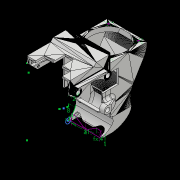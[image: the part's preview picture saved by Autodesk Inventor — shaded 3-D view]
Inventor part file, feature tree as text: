
AUTODESK INVENTOR PART (.ipt)
format: ipt  version: 2018.2 (Build 222227000, 227)  size: 11,716,096 bytes
history: native  units: mm
features: extrude x61, sketch x55, fillet x12, projected_geometry x11, other x3, chamfer x1, imported_body x1
ambient origin geometry x8: Origin, YZ Plane, XZ Plane, XY Plane, X Axis, Y Axis, Z Axis, Center Point
bodies: Body1 (feature_tree)
feature tree (144):
  other  "ソリッド1"
  extrude  "押し出し1"  Depth=10.0mm TaperAngle=0.0deg
  extrude  "押し出し2"  Depth=10.0mm TaperAngle=0.0deg
  sketch  "スケッチ3"
  extrude  "押し出し3"  Depth=15.0mm TaperAngle=0.0deg
  extrude  "押し出し4"  Depth=10.0mm TaperAngle=0.0deg
  sketch  "スケッチ6"
  extrude  "押し出し5"  Depth=5.0mm
  sketch  "スケッチ7"
  extrude  "押し出し6"  Depth=4.5mm
  extrude  "押し出し7"  Depth=10.0mm TaperAngle=0.0deg
  extrude  "押し出し8"  Depth=16.006008mm
  extrude  "押し出し9"  Depth=11.988854mm
  sketch  "スケッチ14"
  extrude  "押し出し10"  Depth=8.0mm
  extrude  "押し出し11"  Depth=10.0mm TaperAngle=0.0deg
  extrude  "押し出し12"  Depth=12.0mm
  extrude  "押し出し13"  Depth=40.0mm TaperAngle=0.0deg
  extrude  "押し出し15"  Depth=0.01mm TaperAngle=0.0deg
  sketch  "スケッチ20"
  sketch  "スケッチ21"
  extrude  "押し出し16"  Depth=0.01mm TaperAngle=0.0deg
  extrude  "押し出し17"  Depth=0.01mm TaperAngle=0.0deg
  extrude  "押し出し18"  Depth=2.0mm
  extrude  "押し出し19"  Depth=1.5mm
  extrude  "押し出し20"  Depth=2.0mm
  extrude  "押し出し21"  Depth=3.0mm
  extrude  "押し出し22"  Depth=10.0mm TaperAngle=0.0deg
  fillet  "フィレット7"  Radius=0.01mm
  extrude  "押し出し23"  Depth=2.0mm TaperAngle=0.0deg
  fillet  "フィレット8"  Radius=1.0mm
  extrude  "押し出し24"  Depth=1.0mm TaperAngle=0.0deg
  chamfer  "面取り2"  Distance=0.5mm
  extrude  "押し出し25"  Depth=0.5mm
  extrude  "押し出し26"  Depth=3.0mm
  other  "作業平面1"
  sketch  "スケッチ34"
  extrude  "押し出し27"  Depth=38.5mm TaperAngle=0.0deg
  extrude  "押し出し28"  Depth=4.0mm
  extrude  "押し出し29"  Depth=4.0mm
  extrude  "押し出し30"  Depth=9.0mm
  extrude  "押し出し31"  Depth=9.0mm
  extrude  "押し出し32"  Depth=2.0mm
  sketch  "スケッチ41"
  extrude  "押し出し36"  Depth=1.0mm TaperAngle=0.0deg
  extrude  "押し出し37"  Depth=1.0mm TaperAngle=0.0deg
  extrude  "押し出し38"  Depth=1.0mm
  fillet  "フィレット12"  Radius=15.5mm
  fillet  "フィレット13"  Radius=17.0mm
  extrude  "押し出し39"  Depth=1.5mm TaperAngle=0.0deg
  extrude  "押し出し43"  Depth=1.5mm TaperAngle=0.0deg
  fillet  "フィレット14"  Radius=10.0mm
  extrude  "押し出し44"  Depth=1.5mm TaperAngle=0.0deg
  fillet  "フィレット17"  Radius=0.5mm
  extrude  "押し出し47"  Depth=8.0mm
  fillet  "フィレット18"  Radius=8.0mm
  extrude  "押し出し48"  Depth=1.5mm TaperAngle=0.0deg
  extrude  "押し出し49"  Depth=0.3mm
  extrude  "押し出し51"  Depth=10.0mm TaperAngle=0.0deg
  extrude  "押し出し52"  Depth=4.5mm TaperAngle=45.0deg
  extrude  "押し出し50"  Depth=0.5mm
  extrude  "押し出し53"  Depth=0.5mm
  extrude  "押し出し54"  Depth=10.0mm TaperAngle=0.0deg
  extrude  "押し出し57"  Depth=1.0mm
  extrude  "押し出し58"  Depth=0.5mm
  extrude  "押し出し55"  Depth=10.0mm TaperAngle=0.0deg
  fillet  "フィレット19"  Radius=3.5mm
  sketch  "スケッチ64"
  extrude  "押し出し59"  Depth=6.0mm
  extrude  "押し出し60"  Depth=1.5mm
  fillet  "フィレット20"  Radius=10.0mm
  fillet  "フィレット21"  Radius=10.0mm
  extrude  "押し出し61"  Depth=1.5mm
  extrude  "押し出し62"  Depth=10.0mm TaperAngle=0.0deg
  extrude  "押し出し64"  Depth=2.0mm
  extrude  "押し出し65"  Depth=10.0mm TaperAngle=0.0deg
  extrude  "押し出し66"  Depth=1.65mm
  fillet  "フィレット25"  Radius=1.65mm
  extrude  "押し出し67"  Depth=1.65mm
  extrude  "押し出し68"  Depth=1.65mm
  extrude  "押し出し69"  Depth=10.0mm TaperAngle=0.0deg
  extrude  "押し出し70"  Depth=10.0mm TaperAngle=0.0deg
  extrude  "押し出し71"  Depth=8.0mm
  sketch  "スケッチ77"
  extrude  "押し出し72"  Depth=10.0mm TaperAngle=0.0deg
  fillet  "フィレット26"  Radius=4.5mm
  sketch  "スケッチ1"
  sketch  "スケッチ2"
  sketch  "スケッチ8"
  other  "ソリッド2"
  sketch  "スケッチ11"
  projected_geometry  "投影ループ1"
  sketch  "スケッチ15"
  projected_geometry  "投影ループ2"
  sketch  "スケッチ16"
  sketch  "スケッチ17"
  projected_geometry  "投影ループ3"
  sketch  "スケッチ19"
  sketch  "スケッチ22"
  sketch  "スケッチ23"
  sketch  "スケッチ24"
  sketch  "スケッチ25"
  sketch  "スケッチ26"
  sketch  "スケッチ27"
  sketch  "スケッチ28"
  sketch  "スケッチ29"
  sketch  "スケッチ31"
  projected_geometry  "投影ループ5"
  sketch  "スケッチ32"
  sketch  "スケッチ33"
  sketch  "スケッチ35"
  sketch  "スケッチ36"
  sketch  "スケッチ37"
  sketch  "スケッチ42"
  sketch  "スケッチ43"
  sketch  "スケッチ45"
  sketch  "スケッチ49"
  sketch  "スケッチ50"
  sketch  "スケッチ54"
  sketch  "スケッチ55"
  sketch  "スケッチ56"
  sketch  "スケッチ58"
  sketch  "スケッチ59"
  sketch  "スケッチ62"
  sketch  "スケッチ63"
  projected_geometry  "投影ループ10"
  projected_geometry  "投影ループ11"
  sketch  "スケッチ65"
  sketch  "スケッチ66"
  sketch  "スケッチ67"
  projected_geometry  "投影ループ14"
  projected_geometry  "投影ループ15"
  sketch  "スケッチ71"
  sketch  "スケッチ72"
  sketch  "スケッチ73"
  sketch  "スケッチ74"
  projected_geometry  "投影ループ17"
  sketch  "スケッチ75"
  projected_geometry  "投影ループ18"
  sketch  "スケッチ76"
  sketch  "スケッチ78"
  projected_geometry  "投影ループ19"
  imported_body  "Base1"
  sketch  "スケッチ57"
